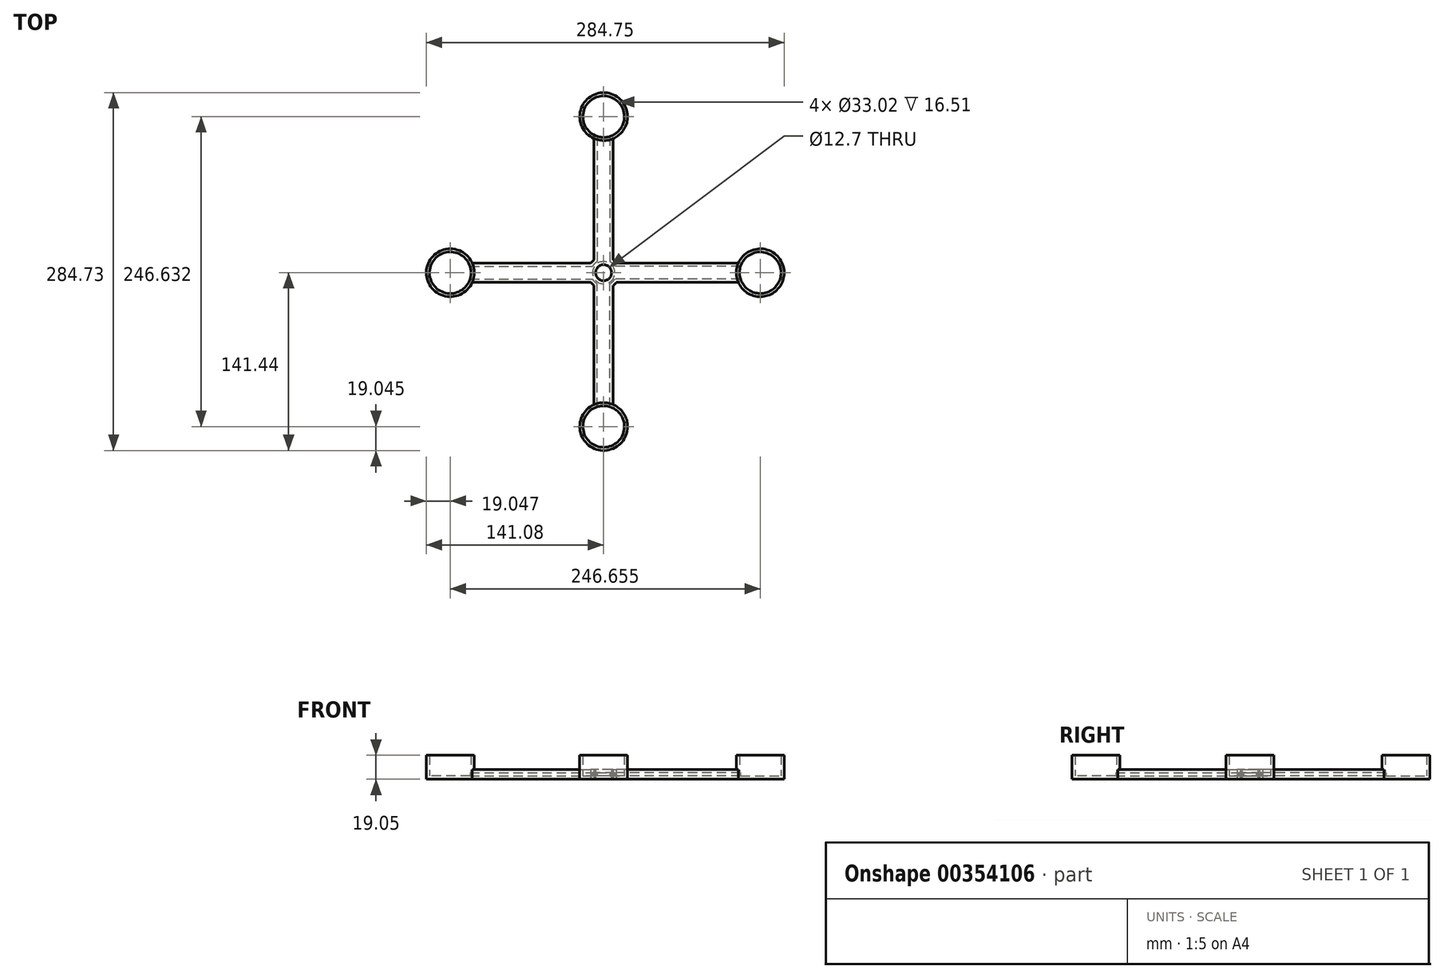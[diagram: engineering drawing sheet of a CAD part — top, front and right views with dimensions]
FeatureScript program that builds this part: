
annotation { "Feature Type Name" : "Feature", "Feature Type Description" : "" }
export const myFeature = defineFeature(function(context is Context, id is Id, definition is map)
    precondition{}
    {
        {
            var Q0;
            Q0=qCreatedBy(makeId("Top.planeOp"),FACE);
            var sketch = newSketch(context, id + "F0", { "sketchPlane" : qUnion([Q0])});
            skCircle(sketch, "E0", {"center": v(0, 0) * mm, "radius": 5 * mm});
            skCircle(sketch, "E1", {"center": v(0, 0) * mm, "radius": 3.5 * mm});
            skSolve(sketch);
        }
        {
            var Q0;
            Q0 = qSketchRegion(id + "F0", true);
            extrude(context, id + "F1", {"entities" : qUnion([Q0]), "depth" : 15 * mm});
        }
        {
            var Q0;
            Q0=makeQuery(id+"F1.opExtrude","SWEPT_BODY",BODY,{"disambiguationData":[OSD([sQuery(id+"F0.wireOp",EDGE,"E0"),sQuery(id+"F0.wireOp",EDGE,"E1")])]});
            deleteBodies(context, id + "F2", {"entities" : qUnion([Q0])});
        }
        {
            var Q0;
            Q0=qCreatedBy(makeId("Front.planeOp"),FACE);
            var sketch = newSketch(context, id + "F3", { "sketchPlane" : qUnion([Q0])});
            skCircle(sketch, "E2", {"center": v(0, 0) * mm, "radius": 6.35 * mm});
            skCircle(sketch, "E3", {"center": v(0, 0) * mm, "radius": 12.7 * mm});
            skPoint(sketch, "E4.middle", {"position": v(12.7, 0) * mm});
            skLineSegment(sketch, "E5", {"start": v(-88.9, 0) * mm, "end": v(-88.9, 5.08) * mm});
            skLineSegment(sketch, "E6", {"start": v(-88.9, 0) * mm, "end": v(-88.9, -5.08) * mm});
            skLineSegment(sketch, "E7", {"start": v(88.9, 0) * mm, "end": v(88.9, -5.08) * mm});
            skLineSegment(sketch, "E8", {"start": v(88.9, 0) * mm, "end": v(88.9, 5.08) * mm});
            skLineSegment(sketch, "E9", {"start": v(0, 88.9) * mm, "end": v(5.08, 88.9) * mm});
            skLineSegment(sketch, "E10", {"start": v(0, 88.9) * mm, "end": v(-5.08, 88.9) * mm});
            skLineSegment(sketch, "E11", {"start": v(0, -88.9) * mm, "end": v(5.08, -88.9) * mm});
            skLineSegment(sketch, "E12", {"start": v(0, -88.9) * mm, "end": v(-5.08, -88.9) * mm});
            skLineSegment(sketch, "E13", {"start": v(-88.9, -5.08) * mm, "end": v(-11.64, -5.08) * mm});
            skLineSegment(sketch, "E14", {"start": v(-5.08, 88.9) * mm, "end": v(-5.08, 11.64) * mm});
            skLineSegment(sketch, "E15", {"start": v(5.08, 88.9) * mm, "end": v(5.08, 11.64) * mm});
            skLineSegment(sketch, "E16", {"start": v(88.9, 5.08) * mm, "end": v(11.64, 5.08) * mm});
            skLineSegment(sketch, "E17", {"start": v(88.9, -5.08) * mm, "end": v(11.64, -5.08) * mm});
            skLineSegment(sketch, "E18", {"start": v(5.08, -88.9) * mm, "end": v(5.08, -11.64) * mm});
            skLineSegment(sketch, "E19", {"start": v(-5.08, -88.9) * mm, "end": v(-5.08, -11.64) * mm});
            skLineSegment(sketch, "E20", {"start": v(-88.9, 5.08) * mm, "end": v(-11.64, 5.08) * mm});
            skSolve(sketch);
        }
        {
            var Q0;
            Q0 = qSketchRegion(id + "F3", true);
            extrude(context, id + "F4", {"entities" : qUnion([Q0]), "depth" : 7.62 * mm});
        }
        {
            var Q0;
            Q0=makeQuery(id+"F4.opExtrude","SWEPT_BODY",BODY,{"disambiguationData":[OSD([sQuery(id+"F3.wireOp",EDGE,"E2"),sQuery(id+"F3.wireOp",EDGE,"E3"),sQuery(id+"F3.wireOp",EDGE,"E5"),sQuery(id+"F3.wireOp",EDGE,"E6"),sQuery(id+"F3.wireOp",EDGE,"E7"),sQuery(id+"F3.wireOp",EDGE,"E8"),sQuery(id+"F3.wireOp",EDGE,"E9"),sQuery(id+"F3.wireOp",EDGE,"E10"),sQuery(id+"F3.wireOp",EDGE,"E11"),sQuery(id+"F3.wireOp",EDGE,"E12"),sQuery(id+"F3.wireOp",EDGE,"E13"),sQuery(id+"F3.wireOp",EDGE,"E14"),sQuery(id+"F3.wireOp",EDGE,"E15"),sQuery(id+"F3.wireOp",EDGE,"E16"),sQuery(id+"F3.wireOp",EDGE,"E17"),sQuery(id+"F3.wireOp",EDGE,"E18"),sQuery(id+"F3.wireOp",EDGE,"E19"),sQuery(id+"F3.wireOp",EDGE,"E20")])]});
            deleteBodies(context, id + "F5", {"entities" : qUnion([Q0])});
        }
        {
            var Q0;
            Q0=qCreatedBy(makeId("Top.planeOp"),FACE);
            var sketch = newSketch(context, id + "F6", { "sketchPlane" : qUnion([Q0])});
            skCircle(sketch, "E21", {"center": v(0, 0) * mm, "radius": 6.35 * mm});
            skCircle(sketch, "E22", {"center": v(0, 0) * mm, "radius": 12.7 * mm});
            skLineSegment(sketch, "E23", {"start": v(-121.92, 0) * mm, "end": v(-121.92, -7.62) * mm});
            skLineSegment(sketch, "E24", {"start": v(-121.92, 0) * mm, "end": v(-121.92, 7.62) * mm});
            skLineSegment(sketch, "E25", {"start": v(0, 124.46) * mm, "end": v(7.62, 124.46) * mm});
            skLineSegment(sketch, "E26", {"start": v(0, 124.46) * mm, "end": v(-7.62, 124.46) * mm});
            skLineSegment(sketch, "E27", {"start": v(124.46, 0) * mm, "end": v(124.46, 7.62) * mm});
            skLineSegment(sketch, "E28", {"start": v(124.46, 0) * mm, "end": v(124.46, -7.62) * mm});
            skLineSegment(sketch, "E29", {"start": v(0, -121.92) * mm, "end": v(-7.62, -121.92) * mm});
            skLineSegment(sketch, "E30", {"start": v(0, -121.92) * mm, "end": v(7.62, -121.92) * mm});
            skLineSegment(sketch, "E31", {"start": v(-7.62, 124.46) * mm, "end": v(-7.62, 10.16) * mm});
            skLineSegment(sketch, "E32", {"start": v(7.62, 124.46) * mm, "end": v(7.62, 10.16) * mm});
            skLineSegment(sketch, "E33", {"start": v(-121.92, -7.62) * mm, "end": v(-10.16, -7.62) * mm});
            skLineSegment(sketch, "E34", {"start": v(-7.62, -121.92) * mm, "end": v(-7.62, -7.62) * mm});
            skLineSegment(sketch, "E35", {"start": v(7.62, -121.92) * mm, "end": v(7.62, -10.16) * mm});
            skLineSegment(sketch, "E36", {"start": v(124.46, 7.62) * mm, "end": v(10.16, 7.62) * mm});
            skLineSegment(sketch, "E37", {"start": v(124.46, -7.62) * mm, "end": v(10.16, -7.62) * mm});
            skLineSegment(sketch, "E38", {"start": v(-121.92, 7.62) * mm, "end": v(-7.62, 7.62) * mm});
            skSolve(sketch);
        }
        {
            var Q0;
            Q0 = qSketchRegion(id + "F6", true);
            extrude(context, id + "F7", {"entities" : qUnion([Q0]), "depth" : 7.62 * mm});
        }
        {
            var Q0;
            Q0=qCreatedBy(makeId("Top.planeOp"),FACE);
            var sketch = newSketch(context, id + "F8", { "sketchPlane" : qUnion([Q0])});
            skCircle(sketch, "E39", {"center": v(-122.03, 0) * mm, "radius": 19.05 * mm});
            skCircle(sketch, "E40", {"center": v(0, 124.24) * mm, "radius": 19.05 * mm});
            skCircle(sketch, "E41", {"center": v(124.62, 0) * mm, "radius": 19.05 * mm});
            skCircle(sketch, "E42", {"center": v(0, -122.4) * mm, "radius": 19.05 * mm});
            skSolve(sketch);
        }
        {
            var Q0;
            Q0=makeQuery(id+"F8.imprint","IMPRINT",FACE,{"disambiguationData":[TD([[makeQuery(id+"F8.imprint","IMPRINT",EDGE,{"derivedFrom":sQuery(id+"F8.wireOp",EDGE,"E39")}),1.0]])]});
            var Q1;
            Q1=makeQuery(id+"F8.imprint","IMPRINT",FACE,{"disambiguationData":[TD([[makeQuery(id+"F8.imprint","IMPRINT",EDGE,{"derivedFrom":sQuery(id+"F8.wireOp",EDGE,"E40")}),1.0]])]});
            var Q2;
            Q2=makeQuery(id+"F8.imprint","IMPRINT",FACE,{"disambiguationData":[TD([[makeQuery(id+"F8.imprint","IMPRINT",EDGE,{"derivedFrom":sQuery(id+"F8.wireOp",EDGE,"E41")}),1.0]])]});
            var Q3;
            Q3=makeQuery(id+"F8.imprint","IMPRINT",FACE,{"disambiguationData":[TD([[makeQuery(id+"F8.imprint","IMPRINT",EDGE,{"derivedFrom":sQuery(id+"F8.wireOp",EDGE,"E42")}),1.0]])]});
            extrude(context, id + "F9", {"entities" : qUnion([Q0, Q1, Q2, Q3]), "operationType" : NewBodyOperationType.ADD, "depth" : 19.05 * mm});
        }
        {
            var Q0;
            Q0=makeQuery(id+"F9.opExtrude","CAP_FACE",FACE,{"disambiguationData":[OSD([sQuery(id+"F8.wireOp",EDGE,"E40")])],"isStart":false});
            var Q1;
            Q1=makeQuery(id+"F9.opExtrude","CAP_FACE",FACE,{"disambiguationData":[OSD([sQuery(id+"F8.wireOp",EDGE,"E41")])],"isStart":false});
            var Q2;
            Q2=makeQuery(id+"F9.opExtrude","CAP_FACE",FACE,{"disambiguationData":[OSD([sQuery(id+"F8.wireOp",EDGE,"E42")])],"isStart":false});
            var Q3;
            Q3=makeQuery(id+"F9.opExtrude","CAP_FACE",FACE,{"disambiguationData":[OSD([sQuery(id+"F8.wireOp",EDGE,"E39")])],"isStart":false});
            shell(context, id + "F10", {"entities" : qUnion([Q0, Q1, Q2, Q3]), "thickness" : 2.54 * mm});
        }
    });
